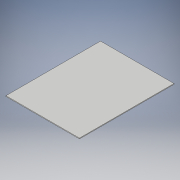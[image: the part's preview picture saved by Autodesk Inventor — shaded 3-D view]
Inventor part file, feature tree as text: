
AUTODESK INVENTOR PART (.ipt)
format: ipt  version: 2019 (Build 230136000, 136)  size: 90,112 bytes
history: native  units: mm
features: other x1, extrude x1, sketch x1
ambient origin geometry x8: Origin, YZ Plane, XZ Plane, XY Plane, X Axis, Y Axis, Z Axis, Center Point
bodies: Body1 (feature_tree)
feature tree (3):
  other  "Těleso1"
  extrude  "Vysunutí1"  Depth=300.0mm
  sketch  "Náčrt1"
